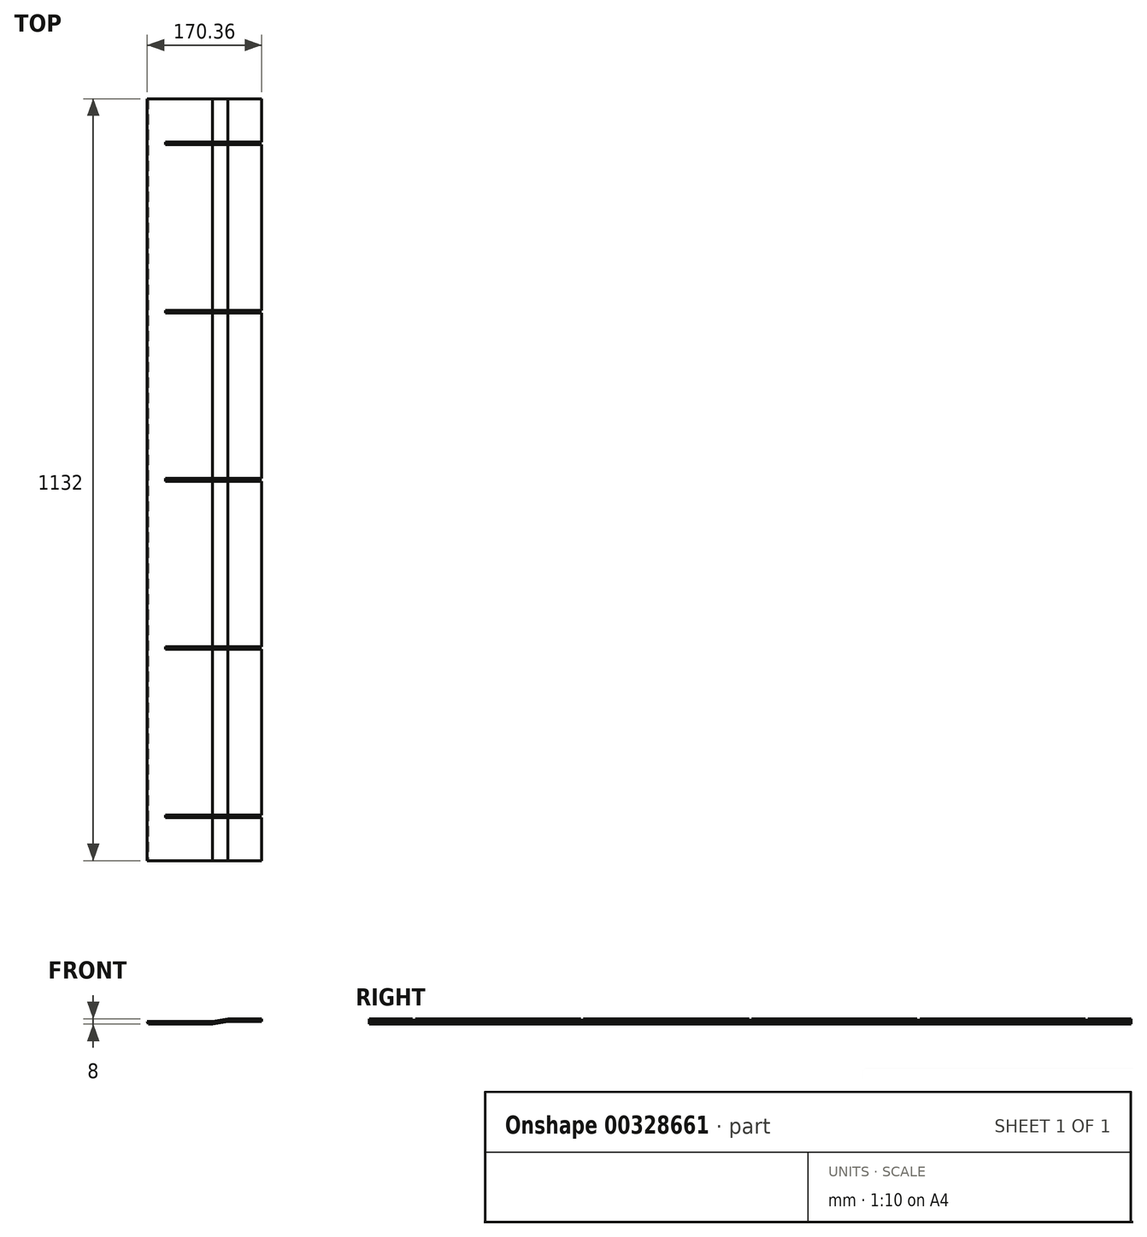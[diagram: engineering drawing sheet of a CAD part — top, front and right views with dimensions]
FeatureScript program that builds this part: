
annotation { "Feature Type Name" : "Feature", "Feature Type Description" : "" }
export const myFeature = defineFeature(function(context is Context, id is Id, definition is map)
    precondition{}
    {
        {
            var Q0;
            Q0=qCreatedBy(makeId("Front.planeOp"),FACE);
            var sketch = newSketch(context, id + "F0", { "sketchPlane" : qUnion([Q0])});
            skLineSegment(sketch, "E0", {"start": v(336, 4) * mm, "end": v(286, 4) * mm});
            skLineSegment(sketch, "E1.trimOffspring", {"start": v(167.3, 0) * mm, "end": v(263.31, 0) * mm});
            skLineSegment(sketch, "E2", {"start": v(336, 4) * mm, "end": v(336, 8) * mm});
            skLineSegment(sketch, "E3", {"start": v(336, 8) * mm, "end": v(285.65, 8) * mm});
            skLineSegment(sketch, "E4", {"start": v(285.65, 8) * mm, "end": v(262.96, 4) * mm});
            skLineSegment(sketch, "E5", {"start": v(263.31, 0) * mm, "end": v(286, 4) * mm});
            skLineSegment(sketch, "E6.trimOffspring", {"start": v(262.96, 4) * mm, "end": v(165.64, 4) * mm});
            skLineSegment(sketch, "E7", {"start": v(167.3, 0) * mm, "end": v(165.64, 4) * mm});
            skSolve(sketch);
        }
        {
            var Q0;
            Q0=qSketchRegion(id+"F0",true);
            extrude(context, id + "F1", {"entities" : qUnion([Q0]), "oppositeDirection" : true, "depth" : 1132 * mm});
        }
        {
            var Q0;
            Q0=makeQuery(id+"F1.opExtrude","SWEPT_FACE",FACE,{"disambiguationData":[OSD([sQuery(id+"F0.wireOp",EDGE,"E6.trimOffspring")])]});
            var sketch = newSketch(context, id + "F2", { "sketchPlane" : qUnion([Q0])});
            skLineSegment(sketch, "E8", {"start": v(193, 64) * mm, "end": v(193, 68) * mm});
            skLineSegment(sketch, "E9", {"start": v(193, 68) * mm, "end": v(336, 68) * mm});
            skLineSegment(sketch, "E10", {"start": v(336, 68) * mm, "end": v(336, 64) * mm});
            skLineSegment(sketch, "E11", {"start": v(336, 64) * mm, "end": v(193, 64) * mm});
            skPoint(sketch, "E12.endSnap0", {"position": v(214.3, 0) * mm});
            skLineSegment(sketch, "E13.0.1.0", {"start": v(336, 318) * mm, "end": v(336, 314) * mm});
            skLineSegment(sketch, "E13.0.1.1", {"start": v(193, 314) * mm, "end": v(193, 318) * mm});
            skLineSegment(sketch, "E13.0.1.2", {"start": v(193, 318) * mm, "end": v(336, 318) * mm});
            skLineSegment(sketch, "E13.0.1.3", {"start": v(336, 314) * mm, "end": v(193, 314) * mm});
            skLineSegment(sketch, "E13.0.2.0", {"start": v(336, 568) * mm, "end": v(336, 564) * mm});
            skLineSegment(sketch, "E13.0.2.1", {"start": v(193, 564) * mm, "end": v(193, 568) * mm});
            skLineSegment(sketch, "E13.0.2.2", {"start": v(193, 568) * mm, "end": v(336, 568) * mm});
            skLineSegment(sketch, "E13.0.2.3", {"start": v(336, 564) * mm, "end": v(193, 564) * mm});
            skLineSegment(sketch, "E13.direction1", {"start": v(193, 64) * mm, "end": v(193, 64) * mm});
            skLineSegment(sketch, "E13.direction2", {"start": v(193, 64) * mm, "end": v(193, 314) * mm, "construction": true});
            skLineSegment(sketch, "E14.0.0.3", {"start": v(336, 818) * mm, "end": v(336, 814) * mm});
            skLineSegment(sketch, "E14.3.0.3", {"start": v(193, 814) * mm, "end": v(193, 818) * mm});
            skLineSegment(sketch, "E14.6.0.3", {"start": v(193, 818) * mm, "end": v(336, 818) * mm});
            skLineSegment(sketch, "E14.9.0.3", {"start": v(336, 814) * mm, "end": v(193, 814) * mm});
            skLineSegment(sketch, "E15.0.0.4", {"start": v(336, 1068) * mm, "end": v(336, 1064) * mm});
            skLineSegment(sketch, "E15.3.0.4", {"start": v(193, 1064) * mm, "end": v(193, 1068) * mm});
            skLineSegment(sketch, "E15.6.0.4", {"start": v(193, 1068) * mm, "end": v(336, 1068) * mm});
            skLineSegment(sketch, "E15.9.0.4", {"start": v(336, 1064) * mm, "end": v(193, 1064) * mm});
            skSolve(sketch);
        }
        {
            var Q0;
            Q0=qSketchRegion(id+"F2",true);
            extrude(context, id + "F3", {"entities" : qUnion([Q0]), "operationType" : NewBodyOperationType.REMOVE, "endBound" : BoundingType.THROUGH_ALL, "oppositeDirection" : true, "depth" : 25 * mm, "hasSecondDirection" : true, "secondDirectionBound" : SecondDirectionBoundingType.THROUGH_ALL, "secondDirectionOppositeDirection" : false, "secondDirectionDepth" : 25 * mm});
        }
    });
